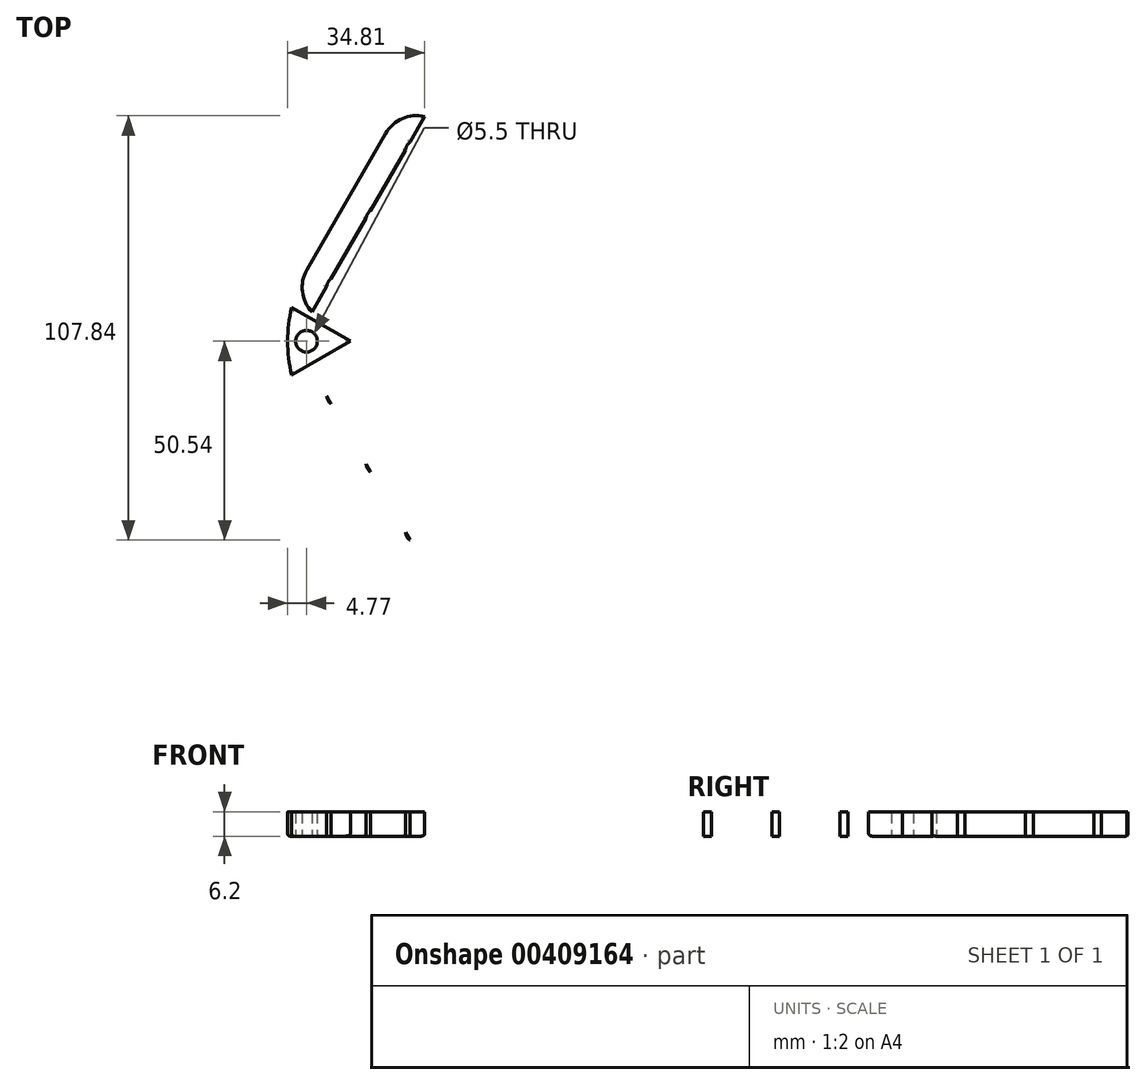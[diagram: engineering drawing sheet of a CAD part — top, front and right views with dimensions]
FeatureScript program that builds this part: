
annotation { "Feature Type Name" : "Feature", "Feature Type Description" : "" }
export const myFeature = defineFeature(function(context is Context, id is Id, definition is map)
    precondition{}
    {
        {
            var Q0;
            Q0=qCreatedBy(makeId("Top.planeOp"),FACE);
            var sketch = newSketch(context, id + "F0", { "sketchPlane" : qUnion([Q0])});
            skLineSegment(sketch, "E0", {"start": v(0, 0) * mm, "end": v(39.56, 68.53) * mm, "construction": true});
            skLineSegment(sketch, "E1", {"start": v(39.56, -68.53) * mm, "end": v(0, 0) * mm, "construction": true});
            skLineSegment(sketch, "E2", {"start": v(-5.77, 10) * mm, "end": v(11.55, 0) * mm, "construction": true});
            skLineSegment(sketch, "E3", {"start": v(11.55, 0) * mm, "end": v(-5.77, -10) * mm, "construction": true});
            skCircle(sketch, "E4", {"center": v(7.89, 13.66) * mm, "radius": 10 * mm, "construction": true});
            skCircle(sketch, "E5", {"center": v(7.89, 13.66) * mm, "radius": 2.75 * mm});
            skCircle(sketch, "E6", {"center": v(17.89, 30.98) * mm, "radius": 2.75 * mm});
            skCircle(sketch, "E7", {"center": v(27.89, 48.3) * mm, "radius": 2.75 * mm});
            skArc(sketch, "E8", {"start": v(0.1, 18.16) * mm, "mid": v(-0.07, 9.46) * mm, "end": v(7.2, 4.69) * mm});
            skArc(sketch, "E9", {"start": v(35.68, 43.8) * mm, "mid": v(32.39, 56.1) * mm, "end": v(20.1, 52.8) * mm});
            skLineSegment(sketch, "E10", {"start": v(0.1, 18.16) * mm, "end": v(20.1, 52.8) * mm});
            skLineSegment(sketch, "E11", {"start": v(17.86, 12.94) * mm, "end": v(15.68, 9.16) * mm, "construction": true});
            skCircle(sketch, "E12.MirrorC", {"center": v(7.89, -13.66) * mm, "radius": 2.75 * mm});
            skCircle(sketch, "E13.MirrorC", {"center": v(17.89, -30.98) * mm, "radius": 2.75 * mm});
            skCircle(sketch, "E14.MirrorC", {"center": v(27.89, -48.3) * mm, "radius": 2.75 * mm});
            skArc(sketch, "E15.MirrorCS", {"start": v(0.1, -18.16) * mm, "mid": v(-0.07, -9.46) * mm, "end": v(7.2, -4.69) * mm});
            skCircle(sketch, "E16.MirrorC", {"center": v(7.89, -13.66) * mm, "radius": 10 * mm, "construction": true});
            skArc(sketch, "E17.MirrorCS", {"start": v(35.68, -43.8) * mm, "mid": v(32.39, -56.1) * mm, "end": v(20.1, -52.8) * mm});
            skLineSegment(sketch, "E18.MirrorCS", {"start": v(0.1, -18.16) * mm, "end": v(20.1, -52.8) * mm});
            skArc(sketch, "E19", {"start": v(7.2, 4.69) * mm, "mid": v(11.55, 0) * mm, "end": v(7.2, -4.69) * mm});
            skArc(sketch, "E20", {"start": v(35.68, 43.8) * mm, "mid": v(23.94, 0) * mm, "end": v(35.68, -43.8) * mm});
            skCircle(sketch, "E21", {"center": v(17.89, 30.98) * mm, "radius": 2.5 * mm, "construction": true});
            skLineSegment(sketch, "E22", {"start": v(34.37, 54.54) * mm, "end": v(5.73, 4.92) * mm});
            skLineSegment(sketch, "E23.MirrorCS", {"start": v(30.04, 57.04) * mm, "end": v(1.4, 7.42) * mm});
            skLineSegment(sketch, "E24.MirrorCS", {"start": v(30.04, -57.04) * mm, "end": v(1.4, -7.42) * mm});
            skLineSegment(sketch, "E25.MirrorCS", {"start": v(34.37, -54.54) * mm, "end": v(5.73, -4.92) * mm});
            skArc(sketch, "E26", {"start": v(0.1, 18.16) * mm, "mid": v(-4.77, 0) * mm, "end": v(0.1, -18.16) * mm});
            skCircle(sketch, "E27", {"center": v(0, 0) * mm, "radius": 2.75 * mm});
            skLineSegment(sketch, "E28", {"start": v(-17, 0) * mm, "end": v(11.55, 0) * mm, "construction": true});
            skLineSegment(sketch, "E29", {"start": v(11.15, 0) * mm, "end": v(-3.74, 8.6) * mm});
            skLineSegment(sketch, "E30.MirrorCS", {"start": v(11.15, 0) * mm, "end": v(-3.74, -8.6) * mm});
            skSolve(sketch);
        }
        {
            var Q0;
            {var subQ4=sQuery(id+"F0.wireOp",EDGE,"E19");Q0=makeQuery(id+"F0.imprint","IMPRINT",FACE,{"disambiguationData":[TD([[makeQuery(id+"F0.imprint","IMPRINT",EDGE,{"derivedFrom":subQ4}),1.0]])]});}
            var Q1;
            {var subQ0=sQuery(id+"F0.wireOp",EDGE,"E10");Q1=makeQuery(id+"F0.imprint","IMPRINT",FACE,{"disambiguationData":[TD([[makeQuery(id+"F0.imprint","IMPRINT",EDGE,{"derivedFrom":subQ0}),-1.0]])]});}
            var Q2;
            {var subQ0=sQuery(id+"F0.wireOp",EDGE,"E23.MirrorCS");var subQ1=sQuery(id+"F0.wireOp",EDGE,"E6");var subQ2=makeQuery(id+"F0.imprint","INTERSECT",VERTEX,{"disambiguationData":[OD(1.0)],"derivedFrom":[subQ1,subQ0]});Q2=makeQuery(id+"F0.imprint","IMPRINT",FACE,{"disambiguationData":[TD([[makeQuery(id+"F0.imprint","IMPRINT",EDGE,{"disambiguationData":[TD([[subQ2,1.0]])],"derivedFrom":subQ1}),-1.0]])]});}
            var Q3;
            {var subQ0=sQuery(id+"F0.wireOp",EDGE,"E23.MirrorCS");var subQ1=sQuery(id+"F0.wireOp",EDGE,"E7");var subQ2=makeQuery(id+"F0.imprint","INTERSECT",VERTEX,{"disambiguationData":[OD(1.0)],"derivedFrom":[subQ1,subQ0]});Q3=makeQuery(id+"F0.imprint","IMPRINT",FACE,{"disambiguationData":[TD([[makeQuery(id+"F0.imprint","IMPRINT",EDGE,{"disambiguationData":[TD([[subQ2,1.0]])],"derivedFrom":subQ1}),-1.0]])]});}
            var Q4;
            {var subQ0=sQuery(id+"F0.wireOp",EDGE,"E23.MirrorCS");var subQ1=sQuery(id+"F0.wireOp",EDGE,"E5");var subQ2=makeQuery(id+"F0.imprint","INTERSECT",VERTEX,{"disambiguationData":[OD(1.0)],"derivedFrom":[subQ1,subQ0]});Q4=makeQuery(id+"F0.imprint","IMPRINT",FACE,{"disambiguationData":[TD([[makeQuery(id+"F0.imprint","IMPRINT",EDGE,{"disambiguationData":[TD([[subQ2,1.0]])],"derivedFrom":subQ1}),-1.0]])]});}
            var Q5;
            {var subQ0=sQuery(id+"F0.wireOp",EDGE,"E23.MirrorCS");var subQ1=sQuery(id+"F0.wireOp",EDGE,"E5");var subQ2=makeQuery(id+"F0.imprint","INTERSECT",VERTEX,{"disambiguationData":[OD(0.0)],"derivedFrom":[subQ1,subQ0]});Q5=makeQuery(id+"F0.imprint","IMPRINT",FACE,{"disambiguationData":[TD([[makeQuery(id+"F0.imprint","IMPRINT",EDGE,{"disambiguationData":[TD([[subQ2,-1.0]])],"derivedFrom":subQ1}),-1.0]])]});}
            var Q6;
            {var subQ0=sQuery(id+"F0.wireOp",EDGE,"E24.MirrorCS");var subQ1=sQuery(id+"F0.wireOp",EDGE,"E12.MirrorC");var subQ2=makeQuery(id+"F0.imprint","INTERSECT",VERTEX,{"disambiguationData":[OD(0.0)],"derivedFrom":[subQ1,subQ0]});Q6=makeQuery(id+"F0.imprint","IMPRINT",FACE,{"disambiguationData":[TD([[makeQuery(id+"F0.imprint","IMPRINT",EDGE,{"disambiguationData":[TD([[subQ2,-1.0]])],"derivedFrom":subQ1}),1.0]])]});}
            var Q7;
            {var subQ0=sQuery(id+"F0.wireOp",EDGE,"E24.MirrorCS");var subQ1=sQuery(id+"F0.wireOp",EDGE,"E12.MirrorC");var subQ2=makeQuery(id+"F0.imprint","INTERSECT",VERTEX,{"disambiguationData":[OD(1.0)],"derivedFrom":[subQ1,subQ0]});Q7=makeQuery(id+"F0.imprint","IMPRINT",FACE,{"disambiguationData":[TD([[makeQuery(id+"F0.imprint","IMPRINT",EDGE,{"disambiguationData":[TD([[subQ2,1.0]])],"derivedFrom":subQ1}),1.0]])]});}
            var Q8;
            {var subQ0=sQuery(id+"F0.wireOp",EDGE,"E24.MirrorCS");var subQ1=sQuery(id+"F0.wireOp",EDGE,"E13.MirrorC");var subQ2=makeQuery(id+"F0.imprint","INTERSECT",VERTEX,{"disambiguationData":[OD(1.0)],"derivedFrom":[subQ1,subQ0]});Q8=makeQuery(id+"F0.imprint","IMPRINT",FACE,{"disambiguationData":[TD([[makeQuery(id+"F0.imprint","IMPRINT",EDGE,{"disambiguationData":[TD([[subQ2,1.0]])],"derivedFrom":subQ1}),1.0]])]});}
            var Q9;
            {var subQ0=sQuery(id+"F0.wireOp",EDGE,"E24.MirrorCS");var subQ1=sQuery(id+"F0.wireOp",EDGE,"E14.MirrorC");var subQ2=makeQuery(id+"F0.imprint","INTERSECT",VERTEX,{"disambiguationData":[OD(1.0)],"derivedFrom":[subQ1,subQ0]});Q9=makeQuery(id+"F0.imprint","IMPRINT",FACE,{"disambiguationData":[TD([[makeQuery(id+"F0.imprint","IMPRINT",EDGE,{"disambiguationData":[TD([[subQ2,1.0]])],"derivedFrom":subQ1}),1.0]])]});}
            var Q10;
            {var subQ0=sQuery(id+"F0.wireOp",EDGE,"E18.MirrorCS");Q10=makeQuery(id+"F0.imprint","IMPRINT",FACE,{"disambiguationData":[TD([[makeQuery(id+"F0.imprint","IMPRINT",EDGE,{"derivedFrom":subQ0}),1.0]])]});}
            var Q11;
            {var subQ3=sQuery(id+"F0.wireOp",EDGE,"E19");Q11=makeQuery(id+"F0.imprint","IMPRINT",FACE,{"disambiguationData":[TD([[makeQuery(id+"F0.imprint","IMPRINT",EDGE,{"derivedFrom":subQ3}),-1.0]])]});}
            var Q12;
            {var subQ1=sQuery(id+"F0.wireOp",EDGE,"E2");var subQ3=sQuery(id+"F0.wireOp",EDGE,"E26");var subQ4=makeQuery(id+"F0.imprint","INTERSECT",VERTEX,{"derivedFrom":[subQ1,subQ3]});Q12=makeQuery(id+"F0.imprint","IMPRINT",FACE,{"disambiguationData":[TD([[makeQuery(id+"F0.imprint","IMPRINT",EDGE,{"disambiguationData":[TD([[subQ4,-1.0]])],"derivedFrom":subQ3}),1.0]])]});}
            extrude(context, id + "F1", {"entities" : qUnion([Q0, Q1, Q2, Q3, Q4, Q5, Q6, Q7, Q8, Q9, Q10, Q11, Q12]), "depth" : 5 * mm, "offsetDistance" : 25 * mm});
        }
        {
            var Q0;
            {var subQ0=sQuery(id+"F0.wireOp",EDGE,"E23.MirrorCS");var subQ1=sQuery(id+"F0.wireOp",EDGE,"E7");var subQ2=makeQuery(id+"F0.imprint","INTERSECT",VERTEX,{"disambiguationData":[OD(1.0)],"derivedFrom":[subQ1,subQ0]});Q0=makeQuery(id+"F0.imprint","IMPRINT",FACE,{"disambiguationData":[TD([[makeQuery(id+"F0.imprint","IMPRINT",EDGE,{"disambiguationData":[TD([[subQ2,1.0]])],"derivedFrom":subQ1}),-1.0]])]});}
            var Q1;
            {var subQ0=sQuery(id+"F0.wireOp",EDGE,"E23.MirrorCS");var subQ1=sQuery(id+"F0.wireOp",EDGE,"E6");var subQ2=makeQuery(id+"F0.imprint","INTERSECT",VERTEX,{"disambiguationData":[OD(1.0)],"derivedFrom":[subQ1,subQ0]});Q1=makeQuery(id+"F0.imprint","IMPRINT",FACE,{"disambiguationData":[TD([[makeQuery(id+"F0.imprint","IMPRINT",EDGE,{"disambiguationData":[TD([[subQ2,1.0]])],"derivedFrom":subQ1}),-1.0]])]});}
            var Q2;
            {var subQ0=sQuery(id+"F0.wireOp",EDGE,"E23.MirrorCS");var subQ1=sQuery(id+"F0.wireOp",EDGE,"E5");var subQ2=makeQuery(id+"F0.imprint","INTERSECT",VERTEX,{"disambiguationData":[OD(1.0)],"derivedFrom":[subQ1,subQ0]});Q2=makeQuery(id+"F0.imprint","IMPRINT",FACE,{"disambiguationData":[TD([[makeQuery(id+"F0.imprint","IMPRINT",EDGE,{"disambiguationData":[TD([[subQ2,1.0]])],"derivedFrom":subQ1}),-1.0]])]});}
            var Q3;
            {var subQ0=sQuery(id+"F0.wireOp",EDGE,"E23.MirrorCS");var subQ1=sQuery(id+"F0.wireOp",EDGE,"E5");var subQ2=makeQuery(id+"F0.imprint","INTERSECT",VERTEX,{"disambiguationData":[OD(0.0)],"derivedFrom":[subQ1,subQ0]});Q3=makeQuery(id+"F0.imprint","IMPRINT",FACE,{"disambiguationData":[TD([[makeQuery(id+"F0.imprint","IMPRINT",EDGE,{"disambiguationData":[TD([[subQ2,-1.0]])],"derivedFrom":subQ1}),-1.0]])]});}
            var Q4;
            {var subQ0=sQuery(id+"F0.wireOp",EDGE,"E24.MirrorCS");var subQ1=sQuery(id+"F0.wireOp",EDGE,"E12.MirrorC");var subQ2=makeQuery(id+"F0.imprint","INTERSECT",VERTEX,{"disambiguationData":[OD(0.0)],"derivedFrom":[subQ1,subQ0]});Q4=makeQuery(id+"F0.imprint","IMPRINT",FACE,{"disambiguationData":[TD([[makeQuery(id+"F0.imprint","IMPRINT",EDGE,{"disambiguationData":[TD([[subQ2,-1.0]])],"derivedFrom":subQ1}),1.0]])]});}
            var Q5;
            {var subQ0=sQuery(id+"F0.wireOp",EDGE,"E24.MirrorCS");var subQ1=sQuery(id+"F0.wireOp",EDGE,"E12.MirrorC");var subQ2=makeQuery(id+"F0.imprint","INTERSECT",VERTEX,{"disambiguationData":[OD(1.0)],"derivedFrom":[subQ1,subQ0]});Q5=makeQuery(id+"F0.imprint","IMPRINT",FACE,{"disambiguationData":[TD([[makeQuery(id+"F0.imprint","IMPRINT",EDGE,{"disambiguationData":[TD([[subQ2,1.0]])],"derivedFrom":subQ1}),1.0]])]});}
            var Q6;
            {var subQ0=sQuery(id+"F0.wireOp",EDGE,"E24.MirrorCS");var subQ1=sQuery(id+"F0.wireOp",EDGE,"E13.MirrorC");var subQ2=makeQuery(id+"F0.imprint","INTERSECT",VERTEX,{"disambiguationData":[OD(1.0)],"derivedFrom":[subQ1,subQ0]});Q6=makeQuery(id+"F0.imprint","IMPRINT",FACE,{"disambiguationData":[TD([[makeQuery(id+"F0.imprint","IMPRINT",EDGE,{"disambiguationData":[TD([[subQ2,1.0]])],"derivedFrom":subQ1}),1.0]])]});}
            var Q7;
            {var subQ0=sQuery(id+"F0.wireOp",EDGE,"E24.MirrorCS");var subQ1=sQuery(id+"F0.wireOp",EDGE,"E14.MirrorC");var subQ2=makeQuery(id+"F0.imprint","INTERSECT",VERTEX,{"disambiguationData":[OD(1.0)],"derivedFrom":[subQ1,subQ0]});Q7=makeQuery(id+"F0.imprint","IMPRINT",FACE,{"disambiguationData":[TD([[makeQuery(id+"F0.imprint","IMPRINT",EDGE,{"disambiguationData":[TD([[subQ2,1.0]])],"derivedFrom":subQ1}),1.0]])]});}
            var Q8;
            {var subQ1=sQuery(id+"F0.wireOp",EDGE,"E2");var subQ3=sQuery(id+"F0.wireOp",EDGE,"E26");var subQ4=makeQuery(id+"F0.imprint","INTERSECT",VERTEX,{"derivedFrom":[subQ1,subQ3]});Q8=makeQuery(id+"F0.imprint","IMPRINT",FACE,{"disambiguationData":[TD([[makeQuery(id+"F0.imprint","IMPRINT",EDGE,{"disambiguationData":[TD([[subQ4,-1.0]])],"derivedFrom":subQ3}),1.0]])]});}
            extrude(context, id + "F2", {"entities" : qUnion([Q0, Q1, Q2, Q3, Q4, Q5, Q6, Q7, Q8]), "operationType" : NewBodyOperationType.ADD, "oppositeDirection" : true, "depth" : 1.2 * mm, "offsetDistance" : 25 * mm});
        }
        {
            var Q0;
            Q0=makeQuery(id+"F2.opExtrude","CAP_FACE",FACE,{"disambiguationData":[OSD([sQuery(id+"F0.wireOp",EDGE,"E6"),sQuery(id+"F0.wireOp",EDGE,"E7"),sQuery(id+"F0.wireOp",EDGE,"E22"),sQuery(id+"F0.wireOp",EDGE,"E23.MirrorCS")])],"isStart":false});
            var Q1;
            Q1=makeQuery(id+"F2.opExtrude","CAP_FACE",FACE,{"disambiguationData":[OSD([sQuery(id+"F0.wireOp",EDGE,"E7"),sQuery(id+"F0.wireOp",EDGE,"E9"),sQuery(id+"F0.wireOp",EDGE,"E22"),sQuery(id+"F0.wireOp",EDGE,"E23.MirrorCS")])],"isStart":false});
            var Q2;
            Q2=makeQuery(id+"F2.opExtrude","CAP_FACE",FACE,{"disambiguationData":[OSD([sQuery(id+"F0.wireOp",EDGE,"E5"),sQuery(id+"F0.wireOp",EDGE,"E6"),sQuery(id+"F0.wireOp",EDGE,"E22"),sQuery(id+"F0.wireOp",EDGE,"E23.MirrorCS")])],"isStart":false});
            var Q3;
            Q3=makeQuery(id+"F2.opExtrude","CAP_FACE",FACE,{"disambiguationData":[OSD([sQuery(id+"F0.wireOp",EDGE,"E5"),sQuery(id+"F0.wireOp",EDGE,"E8"),sQuery(id+"F0.wireOp",EDGE,"E22"),sQuery(id+"F0.wireOp",EDGE,"E23.MirrorCS")])],"isStart":false});
            var Q4;
            Q4=makeQuery(id+"F2.opExtrude","CAP_FACE",FACE,{"disambiguationData":[OSD([sQuery(id+"F0.wireOp",EDGE,"E12.MirrorC"),sQuery(id+"F0.wireOp",EDGE,"E15.MirrorCS"),sQuery(id+"F0.wireOp",EDGE,"E24.MirrorCS"),sQuery(id+"F0.wireOp",EDGE,"E25.MirrorCS")])],"isStart":false});
            var Q5;
            Q5=makeQuery(id+"F2.opExtrude","CAP_FACE",FACE,{"disambiguationData":[OSD([sQuery(id+"F0.wireOp",EDGE,"E12.MirrorC"),sQuery(id+"F0.wireOp",EDGE,"E13.MirrorC"),sQuery(id+"F0.wireOp",EDGE,"E24.MirrorCS"),sQuery(id+"F0.wireOp",EDGE,"E25.MirrorCS")])],"isStart":false});
            var Q6;
            Q6=makeQuery(id+"F2.opExtrude","CAP_FACE",FACE,{"disambiguationData":[OSD([sQuery(id+"F0.wireOp",EDGE,"E14.MirrorC"),sQuery(id+"F0.wireOp",EDGE,"E17.MirrorCS"),sQuery(id+"F0.wireOp",EDGE,"E24.MirrorCS"),sQuery(id+"F0.wireOp",EDGE,"E25.MirrorCS")])],"isStart":false});
            var Q7;
            Q7=makeQuery(id+"F2.opExtrude","CAP_FACE",FACE,{"disambiguationData":[OSD([sQuery(id+"F0.wireOp",EDGE,"E13.MirrorC"),sQuery(id+"F0.wireOp",EDGE,"E14.MirrorC"),sQuery(id+"F0.wireOp",EDGE,"E24.MirrorCS"),sQuery(id+"F0.wireOp",EDGE,"E25.MirrorCS")])],"isStart":false});
            var Q8;
            Q8=makeQuery(id+"F2.opExtrude","CAP_FACE",FACE,{"disambiguationData":[OSD([sQuery(id+"F0.wireOp",EDGE,"E2"),sQuery(id+"F0.wireOp",EDGE,"E3"),sQuery(id+"F0.wireOp",EDGE,"E26")])],"isStart":false});
            fillet(context, id + "F3", {"entities" : qUnion([Q0, Q1, Q2, Q3, Q4, Q5, Q6, Q7, Q8]), "radius" : 0.6 * mm, "tangentPropagation" : true, "allowEdgeOverflow" : false});
        }
    });
